# Revit family: ledwaterproof-cla-e_l1550-53w-4000-em1_549013001300
name_source: partatom
category: Leuchten
revit_build: Autodesk Revit 2016 (Build: 20190508_0715(x64)
units: mm (PartAtom-declared; Revit-internal decimal feet)

## family parameters
Basisbauteil = Fläche
Beim Laden mit Abzugskörper schneiden = Nein
Bemaßung runder Anschluss = Durchmesser verwenden
Gemeinsam genutzt = Nein
Lichtquelle = Nein
Raumberechnungspunkt = Nein
Teiletyp = Normal

## types (1)
- LEDWaterproof-CLA-E L1550-53W-4000-EM1 (1 x LED, 6625 lm)
    Approval mark = CE
    Beschreibung = Compact retrofit waterproof luminaire, with removable cover. Flexible installation: possible to wire from the back and sides. Compatible with 2.5mm² wires, 5-wire through wiring possible. Easy, vandalism-proof mounting clips.
    CIE Flux Codes = 41 71 90 91 100
    Control Gear = Electronic ballast
    Height = 86 mm
    Hersteller = OPPLE
    Lamp Light Flux = 6625 lm
    Lamp count = 1
    Lampe = 1 x LED
    Length = 1560 mm
    Luminous efficacy = 125 lm/W
    ModVariant = Nein
    Modell = 549013001300
    Mounting Place = Ceiling
    Mounting Type = Surface mounted
    Number of Poles = 1
    OnlyDefault = Ja
    Power Factor = 1
    Product Name = LEDWaterproof-CLA-E L1550-53W-4000-EM1
    Product group = Waterproof Classic
    ProductGroupID = 346
    Protection Class = Protection class I
    Protection Degree = IP 65
    RLX_Detail_Level = 1
    RlxData = <blob elided: 219581 chars, md5=28019cda>
    Scheinlast = 53 VA
    Socket = socket
    Standby Power = 0 W
    System Light Flux = 6625 lm
    System Power = 53 W
    Typenbild = 549013001300.jpg
    Typenkommentare = Product without accessories
    URL = http://relux.com
    VarID = ---
    Voltage = 0 V
    Vorgabe-Ansicht = 1800 mm
    Weight = 0.00 kg
    Width = 127 mm

## geometry (parser evidence)
native form markers: Blend x4, Sweep x16
no freeform markers — native parametric forms only
